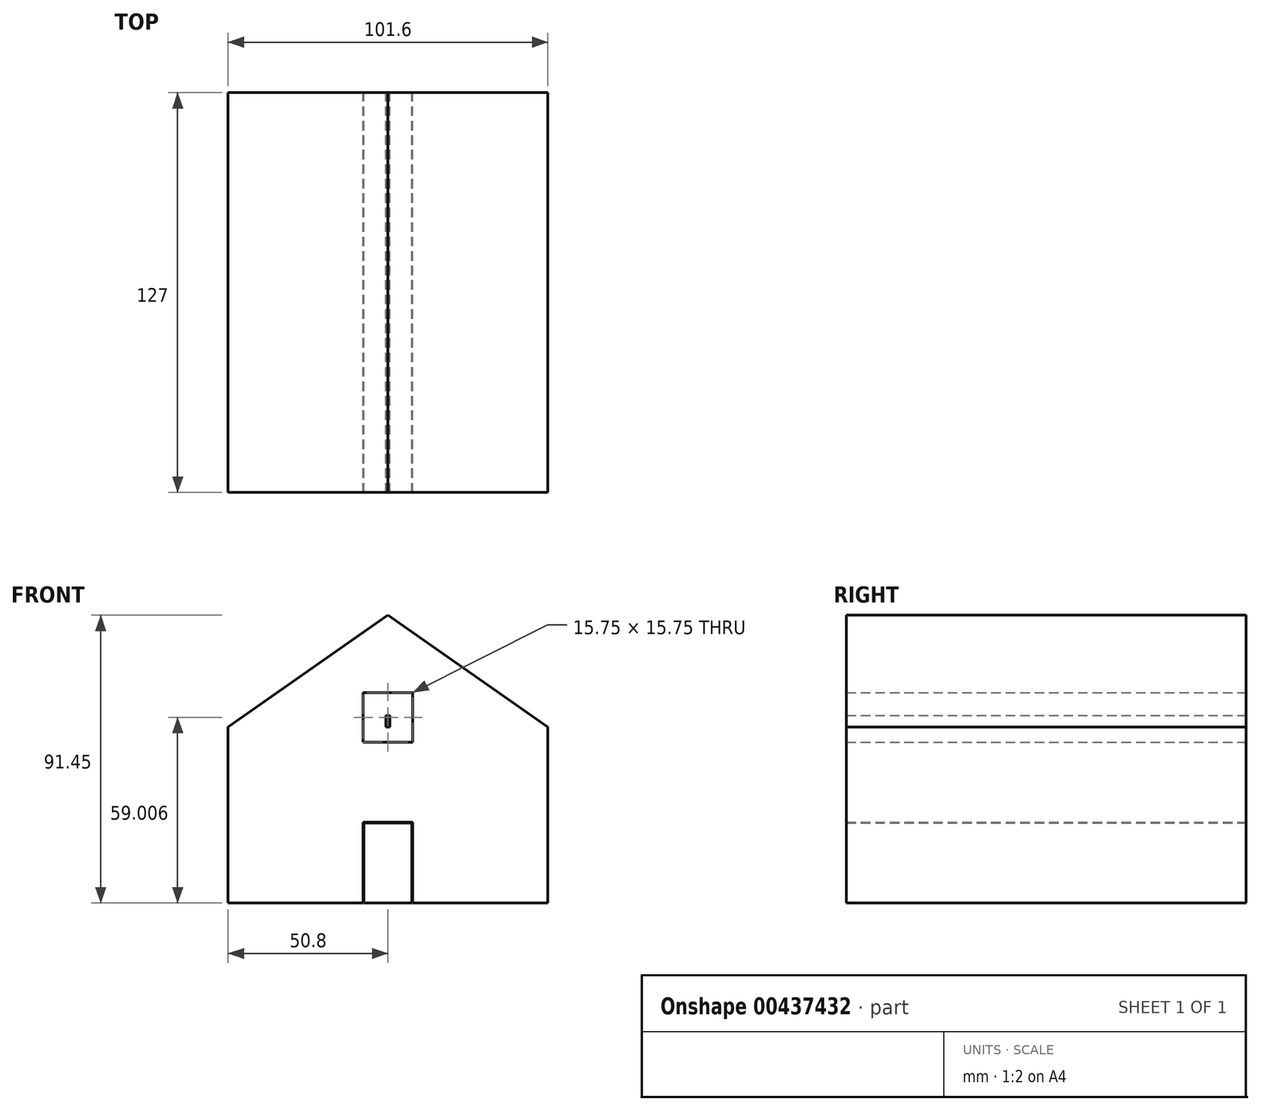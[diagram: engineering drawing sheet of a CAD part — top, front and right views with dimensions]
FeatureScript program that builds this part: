
annotation { "Feature Type Name" : "Feature", "Feature Type Description" : "" }
export const myFeature = defineFeature(function(context is Context, id is Id, definition is map)
    precondition{}
    {
        {
            var Q0;
            Q0=qCreatedBy(makeId("Front.planeOp"),FACE);
            var sketch = newSketch(context, id + "F0", { "sketchPlane" : qUnion([Q0])});
            skLineSegment(sketch, "E0.bottom", {"start": v(-7.62, 0) * mm, "end": v(7.62, 0) * mm});
            skLineSegment(sketch, "E0.top", {"start": v(-7.62, 25.4) * mm, "end": v(7.62, 25.4) * mm});
            skLineSegment(sketch, "E0.left", {"start": v(-7.62, 0) * mm, "end": v(-7.62, 25.4) * mm});
            skLineSegment(sketch, "E0.right", {"start": v(7.62, 0) * mm, "end": v(7.62, 25.4) * mm});
            skPoint(sketch, "E1", {"position": v(4.83, 12.7) * mm});
            skPoint(sketch, "E1.positionSnap0", {"position": v(7.62, 12.7) * mm});
            skLineSegment(sketch, "E2.bottom", {"start": v(-50.8, 0) * mm, "end": v(50.8, 0) * mm});
            skLineSegment(sketch, "E2.top", {"start": v(-50.8, 55.88) * mm, "end": v(50.8, 55.88) * mm});
            skLineSegment(sketch, "E2.left", {"start": v(-50.8, 0) * mm, "end": v(-50.8, 55.88) * mm});
            skLineSegment(sketch, "E2.right", {"start": v(50.8, 0) * mm, "end": v(50.8, 55.88) * mm});
            skLineSegment(sketch, "E3.0", {"start": v(-7.87, 25.65) * mm, "end": v(7.87, 25.65) * mm});
            skLineSegment(sketch, "E3.1", {"start": v(-7.87, -0.25) * mm, "end": v(-7.87, 25.65) * mm});
            skLineSegment(sketch, "E3.3", {"start": v(7.87, -0.25) * mm, "end": v(7.87, 25.65) * mm});
            skLineSegment(sketch, "E4", {"start": v(-61.2, 48.6) * mm, "end": v(0, 91.45) * mm});
            skLineSegment(sketch, "E5", {"start": v(0, 91.45) * mm, "end": v(61.2, 48.6) * mm});
            skLineSegment(sketch, "E6.0", {"start": v(-64.85, 53.8) * mm, "end": v(0, 99.2) * mm});
            skLineSegment(sketch, "E7.MirrorCS", {"start": v(64.85, 53.8) * mm, "end": v(0, 99.2) * mm});
            skLineSegment(sketch, "E8", {"start": v(-64.85, 53.8) * mm, "end": v(-61.2, 48.6) * mm, "construction": true});
            skCircle(sketch, "E9.cCircle", {"center": v(-63.02, 51.2) * mm, "radius": 3.18 * mm, "construction": true});
            skLineSegment(sketch, "E9.0", {"start": v(-66.35, 52.75) * mm, "end": v(-63.34, 54.85) * mm});
            skLineSegment(sketch, "E9.1", {"start": v(-63.34, 54.85) * mm, "end": v(-60.02, 53.3) * mm});
            skLineSegment(sketch, "E9.2", {"start": v(-60.02, 53.3) * mm, "end": v(-59.7, 49.65) * mm});
            skLineSegment(sketch, "E9.3", {"start": v(-59.7, 49.65) * mm, "end": v(-62.7, 47.54) * mm});
            skLineSegment(sketch, "E9.4", {"start": v(-62.7, 47.54) * mm, "end": v(-66.03, 49.1) * mm});
            skLineSegment(sketch, "E9.5", {"start": v(-66.03, 49.1) * mm, "end": v(-66.35, 52.75) * mm});
            skPoint(sketch, "E9.0.midPoint", {"position": v(-64.85, 53.8) * mm});
            skLineSegment(sketch, "E10.MirrorCS", {"start": v(66.35, 52.75) * mm, "end": v(63.34, 54.85) * mm});
            skLineSegment(sketch, "E11.MirrorCS", {"start": v(59.7, 49.65) * mm, "end": v(62.7, 47.54) * mm});
            skLineSegment(sketch, "E12.MirrorCS", {"start": v(62.7, 47.54) * mm, "end": v(66.03, 49.1) * mm});
            skLineSegment(sketch, "E13.MirrorCS", {"start": v(66.03, 49.1) * mm, "end": v(66.35, 52.75) * mm});
            skLineSegment(sketch, "E14.bottom", {"start": v(7.62, 66.63) * mm, "end": v(-7.62, 66.63) * mm});
            skLineSegment(sketch, "E14.top", {"start": v(7.62, 51.39) * mm, "end": v(-7.62, 51.39) * mm});
            skLineSegment(sketch, "E14.left", {"start": v(7.62, 66.63) * mm, "end": v(7.62, 51.39) * mm});
            skLineSegment(sketch, "E14.right", {"start": v(-7.62, 66.63) * mm, "end": v(-7.62, 51.39) * mm});
            skPoint(sketch, "E14.middle", {"position": v(0, 59) * mm});
            skLineSegment(sketch, "E15.bottom", {"start": v(7.87, 66.88) * mm, "end": v(-7.87, 66.88) * mm});
            skLineSegment(sketch, "E15.top", {"start": v(7.87, 51.13) * mm, "end": v(-7.87, 51.13) * mm});
            skLineSegment(sketch, "E15.left", {"start": v(7.87, 66.88) * mm, "end": v(7.87, 51.13) * mm});
            skLineSegment(sketch, "E15.right", {"start": v(-7.87, 66.88) * mm, "end": v(-7.87, 51.13) * mm});
            skLineSegment(sketch, "E16.bottom", {"start": v(-0.64, 66.63) * mm, "end": v(0.63, 66.63) * mm});
            skLineSegment(sketch, "E16.top", {"start": v(-0.64, 51.39) * mm, "end": v(0.63, 51.39) * mm});
            skLineSegment(sketch, "E16.left", {"start": v(-0.64, 66.63) * mm, "end": v(-0.64, 51.39) * mm});
            skLineSegment(sketch, "E16.right", {"start": v(0.64, 66.63) * mm, "end": v(0.64, 51.39) * mm});
            skPoint(sketch, "E17", {"position": v(0, 51.39) * mm});
            skLineSegment(sketch, "E18.bottom", {"start": v(-7.62, 59.64) * mm, "end": v(7.62, 59.64) * mm});
            skLineSegment(sketch, "E18.top", {"start": v(-7.62, 58.37) * mm, "end": v(7.62, 58.37) * mm});
            skLineSegment(sketch, "E18.left", {"start": v(-7.62, 59.64) * mm, "end": v(-7.62, 58.37) * mm});
            skLineSegment(sketch, "E18.right", {"start": v(7.62, 59.64) * mm, "end": v(7.62, 58.37) * mm});
            skPoint(sketch, "E19", {"position": v(-7.62, 59) * mm});
            skLineSegment(sketch, "E20.bottom", {"start": v(-76.2, 0) * mm, "end": v(76.2, 0) * mm});
            skLineSegment(sketch, "E20.top", {"start": v(-76.2, -76.2) * mm, "end": v(76.2, -76.2) * mm});
            skLineSegment(sketch, "E20.left", {"start": v(-76.2, 0) * mm, "end": v(-76.2, -76.2) * mm});
            skLineSegment(sketch, "E20.right", {"start": v(76.2, 0) * mm, "end": v(76.2, -76.2) * mm});
            skPoint(sketch, "E21", {"position": v(0, 0) * mm});
            skSolve(sketch);
        }
        {
            var Q0;
            {var subQ10=sQuery(id+"F0.wireOp",EDGE,"E15.bottom");Q0=makeQuery(id+"F0.imprint","IMPRINT",FACE,{"disambiguationData":[TD([[makeQuery(id+"F0.imprint","IMPRINT",EDGE,{"derivedFrom":subQ10}),-1.0]])]});}
            var Q1;
            {var subQ10=sQuery(id+"F0.wireOp",EDGE,"E2.left");Q1=makeQuery(id+"F0.imprint","IMPRINT",FACE,{"disambiguationData":[TD([[makeQuery(id+"F0.imprint","IMPRINT",EDGE,{"derivedFrom":subQ10}),-1.0]])]});}
            var Q2;
            {var subQ0=sQuery(id+"F0.wireOp",EDGE,"E16.bottom");Q2=makeQuery(id+"F0.imprint","IMPRINT",FACE,{"disambiguationData":[TD([[makeQuery(id+"F0.imprint","IMPRINT",EDGE,{"derivedFrom":subQ0}),-1.0]])]});}
            var Q3;
            {var subQ5=sQuery(id+"F0.wireOp",EDGE,"E18.right");Q3=makeQuery(id+"F0.imprint","IMPRINT",FACE,{"disambiguationData":[TD([[makeQuery(id+"F0.imprint","IMPRINT",EDGE,{"derivedFrom":subQ5}),-1.0]])]});}
            var Q4;
            {var subQ5=sQuery(id+"F0.wireOp",EDGE,"E18.left");Q4=makeQuery(id+"F0.imprint","IMPRINT",FACE,{"disambiguationData":[TD([[makeQuery(id+"F0.imprint","IMPRINT",EDGE,{"derivedFrom":subQ5}),1.0]])]});}
            var Q5;
            {var subQ0=sQuery(id+"F0.wireOp",EDGE,"E18.bottom");var subQ1=sQuery(id+"F0.wireOp",EDGE,"E16.left");var subQ2=makeQuery(id+"F0.imprint","INTERSECT",VERTEX,{"derivedFrom":[subQ1,subQ0]});Q5=makeQuery(id+"F0.imprint","IMPRINT",FACE,{"disambiguationData":[TD([[makeQuery(id+"F0.imprint","IMPRINT",EDGE,{"disambiguationData":[TD([[subQ2,-1.0]])],"derivedFrom":subQ1}),1.0]])]});}
            var Q6;
            {var subQ0=sQuery(id+"F0.wireOp",EDGE,"E16.left");var subQ1=sQuery(id+"F0.wireOp",EDGE,"E2.top");var subQ2=makeQuery(id+"F0.imprint","INTERSECT",VERTEX,{"derivedFrom":[subQ1,subQ0]});Q6=makeQuery(id+"F0.imprint","IMPRINT",FACE,{"disambiguationData":[TD([[makeQuery(id+"F0.imprint","IMPRINT",EDGE,{"disambiguationData":[TD([[subQ2,-1.0]])],"derivedFrom":subQ1}),1.0]])]});}
            var Q7;
            {var subQ5=sQuery(id+"F0.wireOp",EDGE,"E16.top");Q7=makeQuery(id+"F0.imprint","IMPRINT",FACE,{"disambiguationData":[TD([[makeQuery(id+"F0.imprint","IMPRINT",EDGE,{"derivedFrom":subQ5}),1.0]])]});}
            var Q8;
            Q8=makeQuery(id+"F0.imprint","IMPRINT",FACE,{"disambiguationData":[TD([[makeQuery(id+"F0.imprint","IMPRINT",EDGE,{"derivedFrom":sQuery(id+"F0.wireOp",EDGE,"E0.top")}),-1.0]])]});
            extrude(context, id + "F1", {"entities" : qUnion([Q0, Q1, Q2, Q3, Q4, Q5, Q6, Q7, Q8]), "depth" : 127 * mm});
        }
    });
